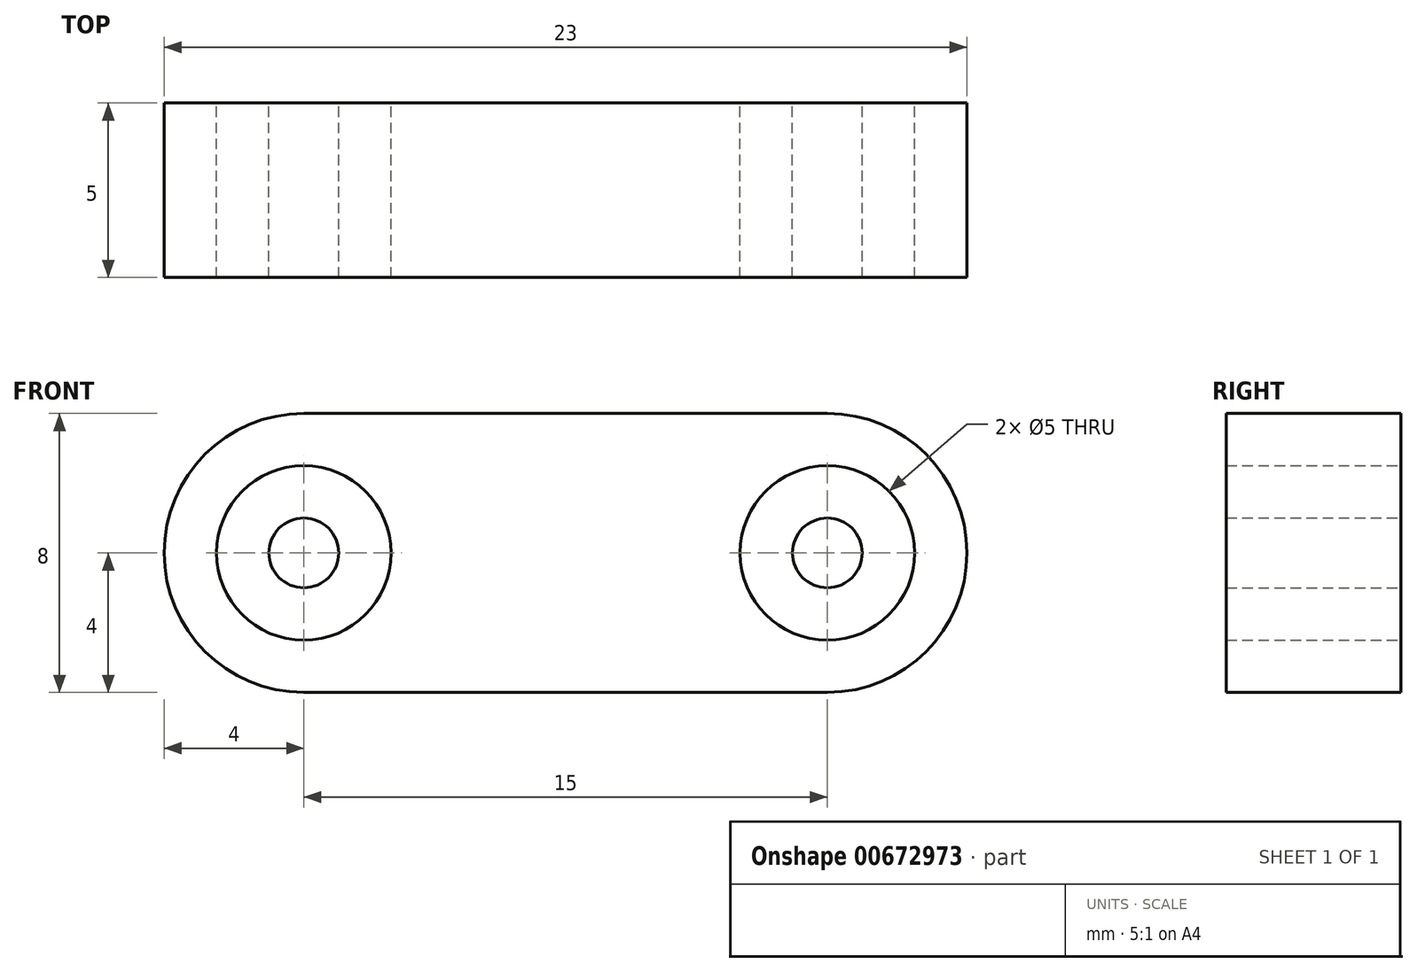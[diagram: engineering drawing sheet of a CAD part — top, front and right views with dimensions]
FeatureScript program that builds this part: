
annotation { "Feature Type Name" : "Feature", "Feature Type Description" : "" }
export const myFeature = defineFeature(function(context is Context, id is Id, definition is map)
    precondition{}
    {
        {
            var Q0;
            Q0=qCreatedBy(makeId("Front.planeOp"),FACE);
            var sketch = newSketch(context, id + "F0", { "sketchPlane" : qUnion([Q0])});
            skArc(sketch, "E0", {"start": v(0, 4) * mm, "mid": v(-4, 0) * mm, "end": v(0, -4) * mm});
            skArc(sketch, "E1", {"start": v(15, -4) * mm, "mid": v(19, 0) * mm, "end": v(15, 4) * mm});
            skCircle(sketch, "E2", {"center": v(15, 0) * mm, "radius": 2.5 * mm});
            skCircle(sketch, "E3", {"center": v(0, 0) * mm, "radius": 2.5 * mm});
            skLineSegment(sketch, "E4", {"start": v(15, -4) * mm, "end": v(0, -4) * mm});
            skLineSegment(sketch, "E5", {"start": v(0, 4) * mm, "end": v(15, 4) * mm});
            skCircle(sketch, "E6", {"center": v(0, 0) * mm, "radius": 1 * mm});
            skCircle(sketch, "E7", {"center": v(15, 0) * mm, "radius": 1 * mm});
            skSolve(sketch);
        }
        {
            var Q0;
            Q0 = qSketchRegion(id + "F0", true);
            var Q1;
            Q1=makeQuery(id+"F0.imprint","IMPRINT",FACE,{"disambiguationData":[TD([[makeQuery(id+"F0.imprint","IMPRINT",EDGE,{"derivedFrom":sQuery(id+"F0.wireOp",EDGE,"E6")}),1.0]])]});
            var Q2;
            Q2=makeQuery(id+"F0.imprint","IMPRINT",FACE,{"disambiguationData":[TD([[makeQuery(id+"F0.imprint","IMPRINT",EDGE,{"derivedFrom":sQuery(id+"F0.wireOp",EDGE,"E7")}),1.0]])]});
            extrude(context, id + "F1", {"entities" : qUnion([Q0, Q1, Q2]), "depth" : 5 * mm, "offsetDistance" : 25 * mm});
        }
    });
